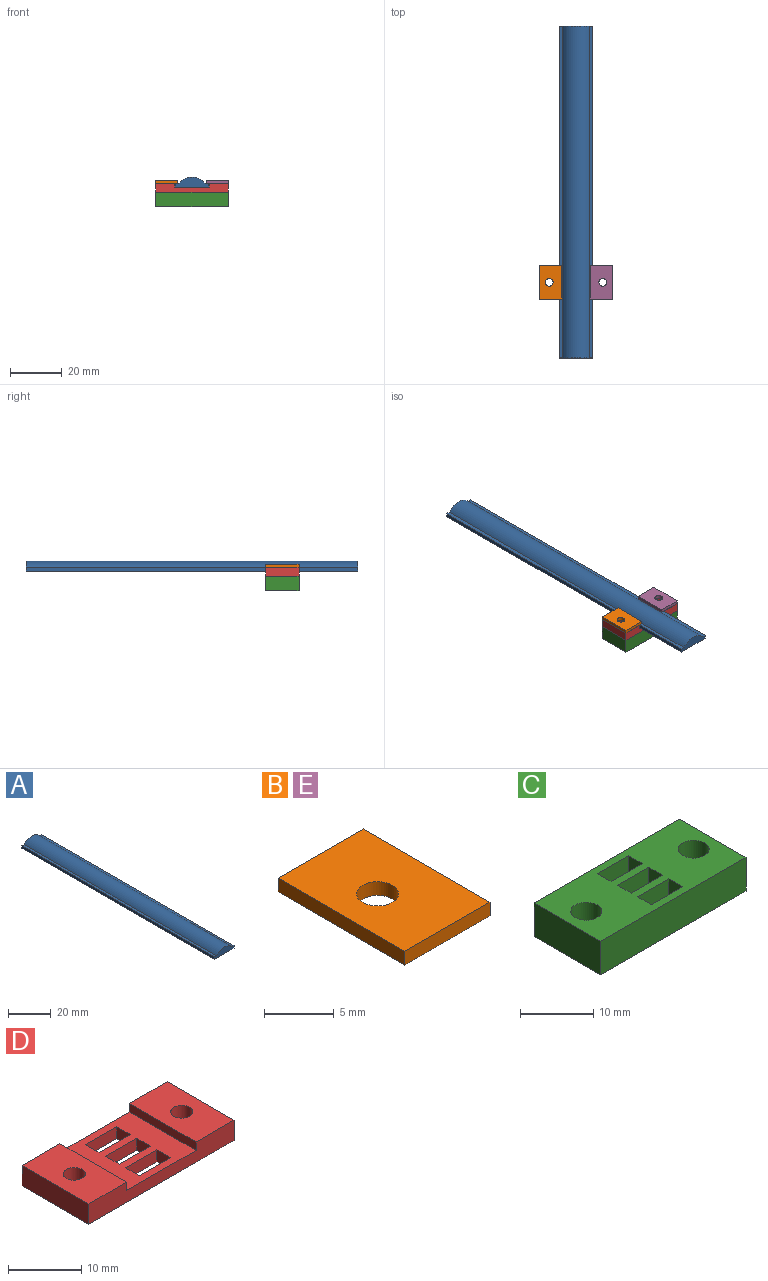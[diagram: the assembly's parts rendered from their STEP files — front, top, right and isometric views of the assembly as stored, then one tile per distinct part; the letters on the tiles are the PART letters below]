
ASSEMBLY  parts=5 mates=4
PART A: 8 faces, bbox 13x128x3.8 mm
  f0: plane 128x1.4mm, normal (-1,0,0), area 179.2mm2, adj f1,f5,f6,f7
  f1: plane 128x13mm, normal (0,0,-1), area 1664mm2, adj f0,f2,f6,f7
  f2: plane 128x1.4mm, normal (1,0,0), area 179.2mm2, adj f1,f3,f6,f7
  f3: plane 128x1.4mm, normal (0,0,1), area 179.2mm2, adj f2,f4,f6,f7
  f4: cylinder r=6.62mm len=128mm, axis (0,1,0), area 1490.5mm2, adj f3,f5,f6,f7
  f5: plane 128x1.4mm, normal (0,0,1), area 179.2mm2, adj f0,f4,f6,f7
  f6: plane 13x3.8mm, normal (0,-1,0), area 35.2mm2, adj f0,f1,f2,f3,f4,f5
  f7: plane 13x3.8mm, normal (0,1,0), area 35.2mm2, adj f0,f1,f2,f3,f4,f5
PART B: 7 faces, bbox 8.6x12.8x1.2 mm
  f0: plane 12.84x1.2mm, normal (-1,0,0), area 15.4mm2, adj f1,f3,f5,f6
  f1: plane 8.6x1.2mm, normal (0,-1,0), area 10.3mm2, adj f0,f2,f5,f6
  f2: plane 12.84x1.2mm, normal (1,0,0), area 15.4mm2, adj f1,f3,f5,f6
  f3: plane 8.6x1.2mm, normal (0,1,0), area 10.3mm2, adj f0,f2,f5,f6
  f4: cylinder r=1.5mm len=3mm, axis (0,0,-1), area 11.3mm2, adj f5,f6
  f5: plane 12.84x8.6mm, normal (0,0,1), area 103.4mm2, adj f0,f1,f2,f3,f4
  f6: plane 12.84x8.6mm, normal (0,0,-1), area 103.4mm2, adj f0,f1,f2,f3,f4
PART C: 20 faces, bbox 28x12.8x5.6 mm
  f0: plane 6x5.6mm, normal (0,-1,0), area 33.6mm2, adj f1,f13,f18,f19
  f1: plane 5.6x2.6mm, normal (-1,0,0), area 14.6mm2, adj f0,f2,f18,f19
  f2: plane 6x5.6mm, normal (0,1,0), area 33.6mm2, adj f1,f13,f18,f19
  f3: plane 5.6x2.6mm, normal (1,0,0), area 14.6mm2, adj f4,f14,f18,f19
  f4: plane 6x5.6mm, normal (0,-1,0), area 33.6mm2, adj f3,f5,f18,f19
  f5: plane 5.6x2.6mm, normal (-1,0,0), area 14.6mm2, adj f4,f14,f18,f19
  f6: plane 6x5.6mm, normal (0,-1,0), area 33.6mm2, adj f7,f15,f18,f19
  f7: plane 5.6x2.6mm, normal (-1,0,0), area 14.6mm2, adj f6,f8,f18,f19
  f8: plane 6x5.6mm, normal (0,1,0), area 33.6mm2, adj f7,f15,f18,f19
  f9: plane 12.84x5.6mm, normal (1,0,0), area 71.9mm2, adj f10,f16,f18,f19
  f10: plane 28x5.6mm, normal (0,1,0), area 156.8mm2, adj f9,f11,f18,f19
  f11: plane 12.84x5.6mm, normal (-1,0,0), area 71.9mm2, adj f10,f16,f18,f19
  f12: cylinder r=2.1mm len=5.6mm, axis (0,0,-1), area 73.9mm2, adj f18,f19
  f13: plane 5.6x2.6mm, normal (1,0,0), area 14.6mm2, adj f0,f2,f18,f19
  f14: plane 6x5.6mm, normal (0,1,0), area 33.6mm2, adj f3,f5,f18,f19
  f15: plane 5.6x2.6mm, normal (1,0,0), area 14.6mm2, adj f6,f8,f18,f19
  f16: plane 28x5.6mm, normal (0,-1,0), area 156.8mm2, adj f9,f11,f18,f19
  f17: cylinder r=2.1mm len=5.6mm, axis (0,0,-1), area 73.9mm2, adj f18,f19
  f18: plane 28x12.84mm, normal (0,0,1), area 285mm2, adj f0,f1,f2,f3,f4,f5,f6,f7
  f19: plane 28x12.84mm, normal (0,0,-1), area 285mm2, adj f0,f1,f2,f3,f4,f5,f6,f7
PART D: 24 faces, bbox 28x12.8x3.4 mm
  f0: plane 28x12.84mm, normal (0,0,-1), area 298.6mm2, adj f2,f3,f8,f9,f10,f11,f12,f13
  f1: plane 13.4x12.84mm, normal (0,0,1), area 125.3mm2, adj f5,f6,f8,f9,f10,f11,f12,f13
  f2: plane 12.84x3.4mm, normal (-1,0,0), area 43.7mm2, adj f0,f7,f8,f9
  f3: plane 12.84x3.4mm, normal (1,0,0), area 43.7mm2, adj f0,f4,f8,f9
  f4: plane 12.84x7.3mm, normal (0,0,1), area 86.7mm2, adj f3,f5,f8,f9,f23
  f5: plane 12.84x1.4mm, normal (-1,0,0), area 18mm2, adj f1,f4,f8,f9
  f6: plane 12.84x1.4mm, normal (1,0,0), area 18mm2, adj f1,f7,f8,f9
  f7: plane 12.84x7.3mm, normal (0,0,1), area 86.7mm2, adj f2,f6,f8,f9,f22
  f8: plane 28x3.4mm, normal (0,-1,0), area 76.4mm2, adj f0,f1,f2,f3,f4,f5,f6,f7
  f9: plane 28x3.4mm, normal (0,1,0), area 76.4mm2, adj f0,f1,f2,f3,f4,f5,f6,f7
  f10: plane 2.6x2mm, normal (-1,0,0), area 5.2mm2, adj f0,f1,f11,f13
  f11: plane 6x2mm, normal (0,-1,0), area 12mm2, adj f0,f1,f10,f12
  f12: plane 2.6x2mm, normal (1,0,0), area 5.2mm2, adj f0,f1,f11,f13
  f13: plane 6x2mm, normal (0,1,0), area 12mm2, adj f0,f1,f10,f12
  f14: plane 2.6x2mm, normal (-1,0,0), area 5.2mm2, adj f0,f1,f15,f17
  f15: plane 6x2mm, normal (0,-1,0), area 12mm2, adj f0,f1,f14,f16
  f16: plane 2.6x2mm, normal (1,0,0), area 5.2mm2, adj f0,f1,f15,f17
  f17: plane 6x2mm, normal (0,1,0), area 12mm2, adj f0,f1,f14,f16
  f18: plane 2.6x2mm, normal (-1,0,0), area 5.2mm2, adj f0,f1,f19,f21
  f19: plane 6x2mm, normal (0,-1,0), area 12mm2, adj f0,f1,f18,f20
  f20: plane 2.6x2mm, normal (1,0,0), area 5.2mm2, adj f0,f1,f19,f21
  f21: plane 6x2mm, normal (0,1,0), area 12mm2, adj f0,f1,f18,f20
  f22: cylinder r=1.5mm len=3.4mm, axis (0,0,1), area 32mm2, adj f0,f7
  f23: cylinder r=1.5mm len=3.4mm, axis (0,0,1), area 32mm2, adj f0,f4
PART E: same geometry as B
PLACE A t=(0,64,0)mm
PLACE B t=(0,-34.84,1.4)mm
PLACE C t=(0,-34.84,-7.6)mm
PLACE D t=(0,-34.84,0)mm
PLACE E rot(axis=(0,0,1),180deg) t=(0,-34.84,1.4)mm
MATE slider D.f9 <-> A.f6  axis (0,1,0) through (0,-28.42,0)mm
MATE fastened C.f12 <-> D.f22  axis (0,0,-1) through (-10.35,-34.84,-2)mm
MATE fastened D.f23 <-> E.f4  axis (0,0,1) through (10.35,-34.84,1.4)mm
MATE fastened B.f4 <-> D.f22  axis (0,0,-1) through (-10.35,-34.84,1.4)mm
